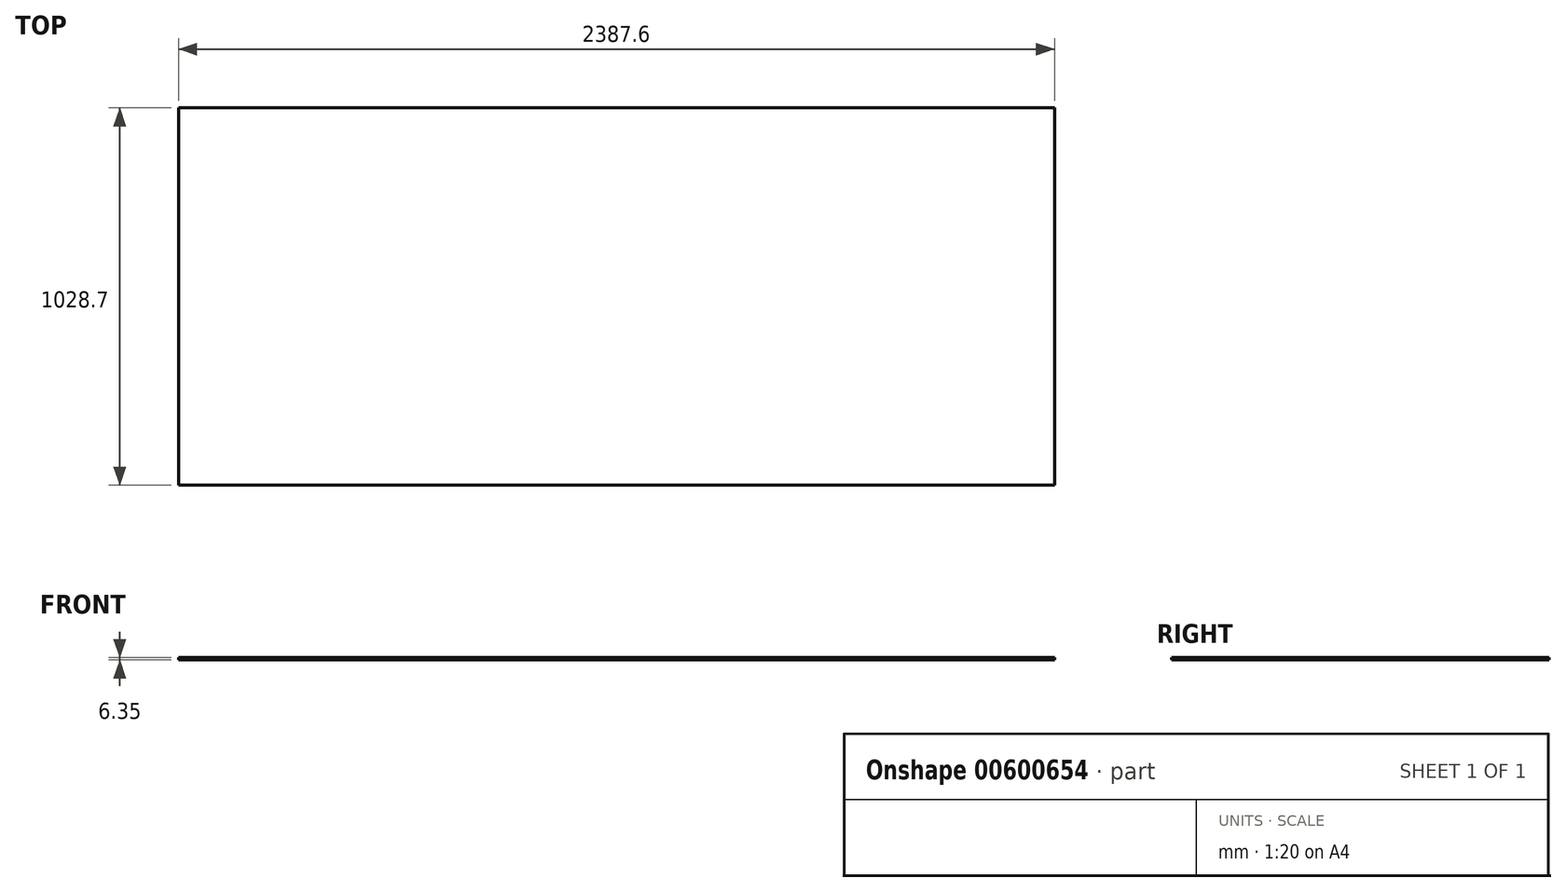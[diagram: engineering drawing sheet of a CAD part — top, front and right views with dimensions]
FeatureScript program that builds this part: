
annotation { "Feature Type Name" : "Feature", "Feature Type Description" : "" }
export const myFeature = defineFeature(function(context is Context, id is Id, definition is map)
    precondition{}
    {
        {
            var Q0;
            Q0=qCreatedBy(makeId("Top.planeOp"),FACE);
            var sketch = newSketch(context, id + "F0", { "sketchPlane" : qUnion([Q0])});
            skLineSegment(sketch, "E0.bottom", {"start": v(1193.8, -514.35) * mm, "end": v(-1193.8, -514.35) * mm});
            skLineSegment(sketch, "E0.top", {"start": v(1193.8, 514.35) * mm, "end": v(-1193.8, 514.35) * mm});
            skLineSegment(sketch, "E0.left", {"start": v(1193.8, -514.35) * mm, "end": v(1193.8, 514.35) * mm});
            skLineSegment(sketch, "E0.right", {"start": v(-1193.8, -514.35) * mm, "end": v(-1193.8, 514.35) * mm});
            skPoint(sketch, "E0.middle", {"position": v(0, 0) * mm});
            skSolve(sketch);
        }
        {
            var Q0;
            Q0=makeQuery(id+"F0.imprint","IMPRINT",FACE,{"disambiguationData":[TD([[makeQuery(id+"F0.imprint","IMPRINT",EDGE,{"derivedFrom":sQuery(id+"F0.wireOp",EDGE,"E0.bottom")}),-1.0]])]});
            extrude(context, id + "F1", {"entities" : qUnion([Q0]), "depth" : 6.35 * mm, "offsetDistance" : 25.4 * mm});
        }
    });
